# Revit family: Legrand Coffret XL³ 400 Métal
name_source: partatom
category: Equipement électrique
units: mm (PartAtom-declared; Revit-internal decimal feet)

## family parameters
Basée sur le plan de construction = Non
Configuration du panneau = Deux colonnes, circuits au sein
Cote de connecteur circulaire = Utiliser le diamètre
Couper avec des vides une fois chargée = Non
Numéro OmniClass = 23.80.30.11.17
Partagée = Non
Point de calcul de pièce = Non
Titre OmniClass = Distribution Boards and Control Panels
Toujours verticalement = Oui
Type d'élément = Tableau de raccordement

## types (8) — shared parameters
Conditions Générale d'Utilisation = https://export.legrand.com
Fabricant = Legrand
Finition = Peinture époxipolyester déposée par poudrage électrostatique
ICW (jusqu'à) (kA) = 25
IK avec porte = 08
IK sans porte = 07
IN max (A) = 400
IP avec porte = 40
IP sans porte = 30
IPK (kA) = 52.5
Largeur (mm) = 575 mm  [stored 1.88648 ft]
Largeur zone d'installation = 1245 mm
Matière = Acier
Matière coin = Plastique
Modèle = XL³ 400 Metal
RAL = 7035
URL = https://www.legrand.fr
profondeur (mm) = 200 mm  [stored 0.656168 ft]
profondeur zone d'installation = 750 mm  [stored 2.46063 ft]
zero-valued in all types: Elévation par défaut

## per-type parameters (varying)
| type | Hauteur | Hauteur totale (mm) | Hauteur zone d'installation | niveau Coffret | plan zone d'installation | poignée Coffret | poignée Tableau | socle |
| 020103-020273 | 600 mm | 600 mm | 600 mm | 0 mm  [stored 0 ft] | 5 mm  [stored 0.0164042 ft] | Oui | Non | Non |
| 020118-020278 | 1500 mm  [stored 4.92126 ft] | 1600 mm  [stored 5.24934 ft] | 1600 mm  [stored 5.24934 ft] | 100 mm  [stored 0.328084 ft] | 0 mm  [stored 0 ft] | Non | Oui | Oui |
| 020104-020274 | 750 mm  [stored 2.46063 ft] | 750 mm  [stored 2.46063 ft] | 750 mm  [stored 2.46063 ft] | 0 mm  [stored 0 ft] | 5 mm  [stored 0.0164042 ft] | Oui | Non | Non |
| 020105-020275 | 900 mm  [stored 2.95276 ft] | 900 mm  [stored 2.95276 ft] | 900 mm  [stored 2.95276 ft] | 0 mm  [stored 0 ft] | 5 mm  [stored 0.0164042 ft] | Oui | Non | Non |
| 020106-020276 | 1050 mm | 1050 mm | 1050 mm | 0 mm  [stored 0 ft] | 5 mm  [stored 0.0164042 ft] | Oui | Non | Non |
| 020107-020277 | 1200 mm | 1200 mm | 1200 mm | 0 mm  [stored 0 ft] | 5 mm  [stored 0.0164042 ft] | Oui | Non | Non |
| 020108-020278 | 1500 mm  [stored 4.92126 ft] | 1500 mm  [stored 4.92126 ft] | 1500 mm  [stored 4.92126 ft] | 0 mm  [stored 0 ft] | 5 mm  [stored 0.0164042 ft] | Oui | Non | Non |
| 020119-020279 | 1800 mm  [stored 5.90551 ft] | 1900 mm  [stored 6.2336 ft] | 1900 mm  [stored 6.2336 ft] | 100 mm  [stored 0.328084 ft] | 0 mm  [stored 0 ft] | Non | Oui | Oui |

note: [stored X ft] marks values corroborated as IEEE doubles in the binary element streams (Revit-internal decimal feet)
